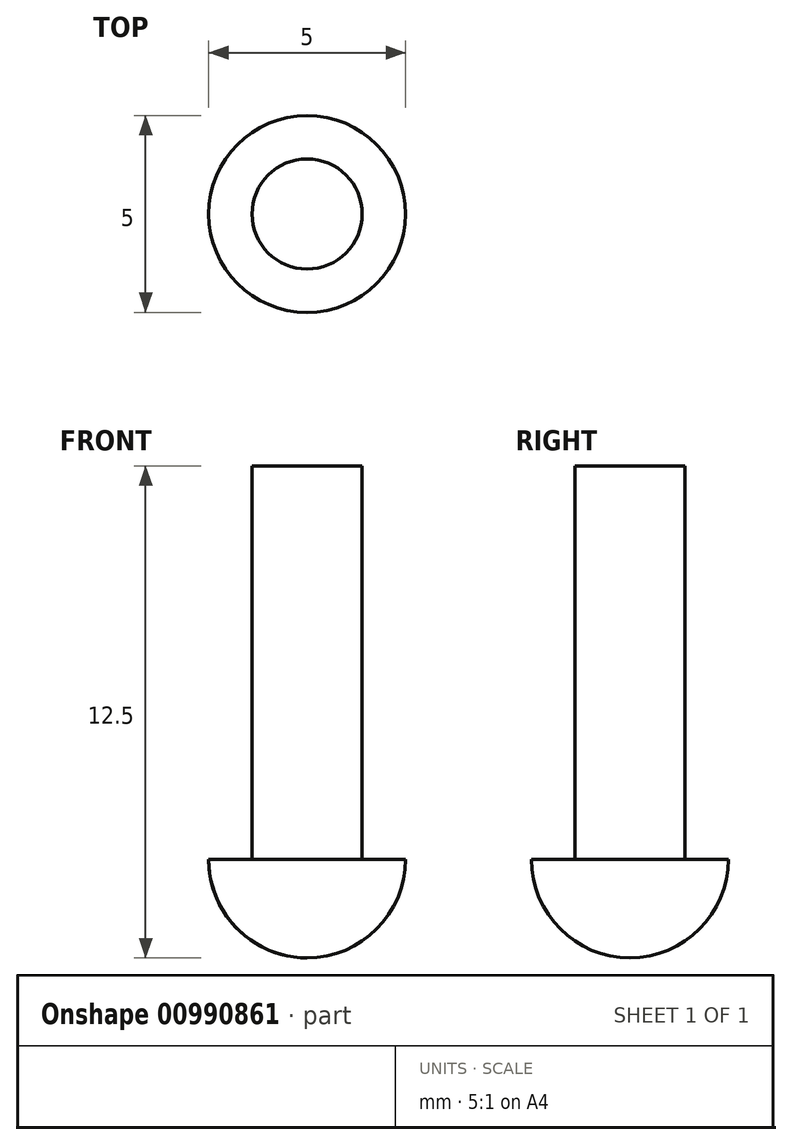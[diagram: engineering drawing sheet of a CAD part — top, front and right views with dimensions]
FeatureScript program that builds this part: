
annotation { "Feature Type Name" : "Feature", "Feature Type Description" : "" }
export const myFeature = defineFeature(function(context is Context, id is Id, definition is map)
    precondition{}
    {
        {
            var Q0;
            Q0=qCreatedBy(makeId("Top.planeOp"),FACE);
            var sketch = newSketch(context, id + "F0", { "sketchPlane" : qUnion([Q0])});
            skCircle(sketch, "E0", {"center": v(0, 0) * mm, "radius": 1.4 * mm});
            skSolve(sketch);
        }
        {
            var Q0;
            Q0=makeQuery(id+"F0.imprint","IMPRINT",FACE,{"disambiguationData":[TD([[makeQuery(id+"F0.imprint","IMPRINT",EDGE,{"derivedFrom":sQuery(id+"F0.wireOp",EDGE,"E0")}),1.0]])]});
            extrude(context, id + "F1", {"entities" : qUnion([Q0]), "depth" : 10 * mm, "offsetDistance" : 25 * mm});
        }
        {
            var Q0;
            Q0=qCreatedBy(makeId("Front.planeOp"),FACE);
            var sketch = newSketch(context, id + "F2", { "sketchPlane" : qUnion([Q0])});
            skArc(sketch, "E1", {"start": v(-2.5, 0) * mm, "mid": v(-1.77, -1.77) * mm, "end": v(0, -2.5) * mm});
            skLineSegment(sketch, "E2", {"start": v(-2.5, 0) * mm, "end": v(0, 0) * mm});
            skLineSegment(sketch, "E3", {"start": v(0, 0) * mm, "end": v(0, -2.5) * mm});
            skSolve(sketch);
        }
        {
            var Q0;
            Q0=makeQuery(id+"F2.imprint","IMPRINT",FACE,{"disambiguationData":[TD([[makeQuery(id+"F2.imprint","IMPRINT",EDGE,{"derivedFrom":sQuery(id+"F2.wireOp",EDGE,"E1")}),1.0]])]});
            var Q1;
            Q1=sQuery(id+"F2.wireOp",EDGE,"E3");
            revolve(context, id + "F3", {"operationType" : NewBodyOperationType.ADD, "surfaceOperationType" : NewSurfaceOperationType.NEW, "entities" : qUnion([Q0]), "axis" : qUnion([Q1]), "revolveType" : RevolveType.FULL});
        }
    });
